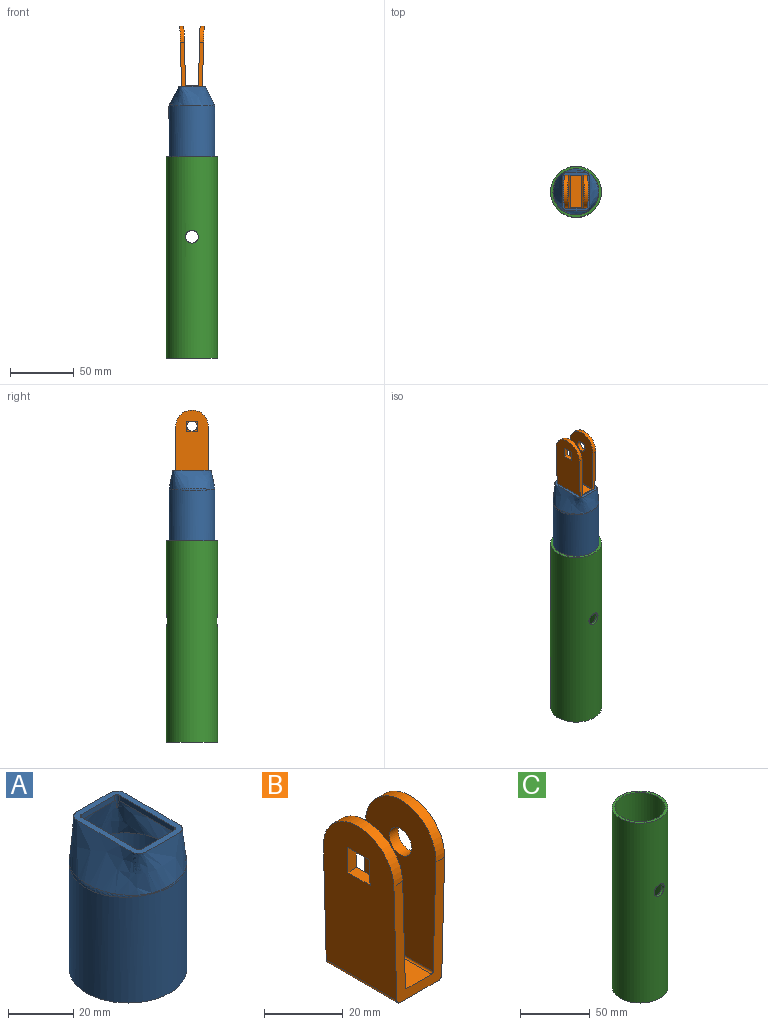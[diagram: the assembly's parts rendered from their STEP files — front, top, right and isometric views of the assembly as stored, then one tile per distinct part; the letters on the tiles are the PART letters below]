
ASSEMBLY  parts=3 mates=2
PART A: 17 faces, bbox 40x40x59 mm
  f0: plane 30.67x21.17mm, normal (0,0,1), area 179.1mm2, adj f4,f8,f9,f10,f11,f12,f13,f14
  f1: plane 25.49x16.68mm, normal (0,0,-1), area 19.9mm2, adj f7,f11,f12,f13,f14,f15
  f2: cylinder r=18mm len=39.87mm, axis (0,0,-1), area 4482.3mm2, adj f3,f16
  f3: plane 36x36mm, normal (0,0,-1), area 213.6mm2, adj f2,f5
  f4: bspline ~35.93x35.85mm, area 1575.2mm2, adj f0,f16
  f5: cylinder r=16mm len=39.91mm, axis (0,0,-1), area 3996.6mm2, adj f3,f7
  f6: plane 25.45x16.71mm, normal (0,0,-1), area 20.4mm2, adj f7,f8,f9,f10,f14,f15
  f7: offset ~39.96x39.92mm, area 1262.9mm2, adj f1,f5,f6,f14,f15
  f8: plane 14.5x2mm, normal (0,-1,0), area 29mm2, adj f0,f6,f9,f15
  f9: cylinder r=1mm len=2mm, axis (0,0,1), area 3.1mm2, adj f0,f6,f8,f10
  f10: plane 24x2mm, normal (1,0,0), area 48mm2, adj f0,f6,f9,f14
  f11: plane 14.5x2mm, normal (0,1,0), area 29mm2, adj f0,f1,f12,f14
  f12: cylinder r=1mm len=2mm, axis (0,0,1), area 3.1mm2, adj f0,f1,f11,f13
  f13: plane 24x2mm, normal (-1,0,0), area 48mm2, adj f0,f1,f12,f15
  f14: cylinder r=1mm len=5.36mm, axis (0,0,1), area 5.8mm2, adj f0,f1,f6,f7,f10,f11
  f15: cylinder r=1mm len=4.78mm, axis (0,0,1), area 5.1mm2, adj f0,f1,f6,f7,f8,f13
  f16: bspline ~35.98x35.97mm, area 84.2mm2, adj f2,f4
PART B: 19 faces, bbox 19x25.4x50.1 mm
  f0: plane 48.77x25.4mm, normal (-1,0,-0.03), area 1105.9mm2, adj f2,f3,f8,f13,f14,f15,f16,f17
  f1: plane 46.39x25.4mm, normal (1,0,0.03), area 1045.6mm2, adj f2,f3,f7,f13,f14,f15,f16,f17
  f2: plane 37.4x18.27mm, normal (0,1,0), area 268.1mm2, adj f0,f1,f4,f5,f6,f7,f8,f9
  f3: plane 37.4x18.27mm, normal (0,-1,0), area 268.1mm2, adj f0,f1,f4,f5,f6,f7,f8,f9
  f4: plane 46.39x25.4mm, normal (-1,0,0.03), area 1059.3mm2, adj f2,f3,f5,f12,f18
  f5: cylinder r=0.54mm len=25.4mm, axis (0,1,0), area 21.1mm2, adj f2,f3,f4,f6
  f6: plane 25.4x8.92mm, normal (0,0,1), area 226.6mm2, adj f2,f3,f5,f7
  f7: cylinder r=0.54mm len=25.4mm, axis (0,1,0), area 21.1mm2, adj f1,f2,f3,f6
  f8: cylinder r=1.27mm len=25.4mm, axis (0,1,0), area 49.7mm2, adj f0,f2,f3,f9
  f9: plane 25.4x13.67mm, normal (0,0,-1), area 347.3mm2, adj f2,f3,f8,f10
  f10: cylinder r=1.27mm len=25.4mm, axis (0,1,0), area 49.7mm2, adj f2,f3,f9,f11
  f11: plane 48.77x25.4mm, normal (1,0,-0.03), area 1119.7mm2, adj f2,f3,f10,f12,f18
  f12: cylinder r=12.7mm len=25.4mm, axis (1,0,-0.03), area 126.7mm2, adj f2,f3,f4,f11
  f13: cylinder r=12.7mm len=25.4mm, axis (-1,0,-0.03), area 126.7mm2, adj f0,f1,f2,f3
  f14: plane 8.09x3.4mm, normal (0,1,0), area 25.4mm2, adj f0,f1,f15,f17
  f15: plane 8x3.17mm, normal (0.03,0,-1), area 25.4mm2, adj f0,f1,f14,f16
  f16: plane 8.09x3.4mm, normal (0,-1,0), area 25.4mm2, adj f0,f1,f15,f17
  f17: plane 8x3.17mm, normal (-0.03,0,1), area 25.4mm2, adj f0,f1,f14,f16
  f18: cylinder r=4mm len=8.09mm, axis (1,0,-0.03), area 79.8mm2, adj f4,f11
PART C: 6 faces, bbox 40x40x157.7 mm
  f0: cylinder r=18mm len=157.73mm, axis (0,0,1), area 17680.2mm2, adj f2,f3,f4,f5
  f1: cylinder r=20mm len=157.73mm, axis (0,0,1), area 19662.9mm2, adj f2,f3,f4,f5
  f2: plane 40x40mm, normal (0,0,-1), area 238.8mm2, adj f0,f1
  f3: plane 40x40mm, normal (0,0,1), area 238.8mm2, adj f0,f1
  f4: cylinder r=5mm len=10mm, axis (0,-1,0), area 64mm2, adj f0,f1
  f5: cylinder r=5mm len=10mm, axis (0,-1,0), area 64mm2, adj f0,f1
PLACE A at identity
PLACE B t=(0,0,52.18)mm
PLACE C at identity fixed
MATE fastened A.f2 <-> C.f0  axis (0,0,-1) through (0,0,0)mm
MATE fastened B.f9 <-> A.f2  axis (0,0,-1) through (0,0,52.18)mm
